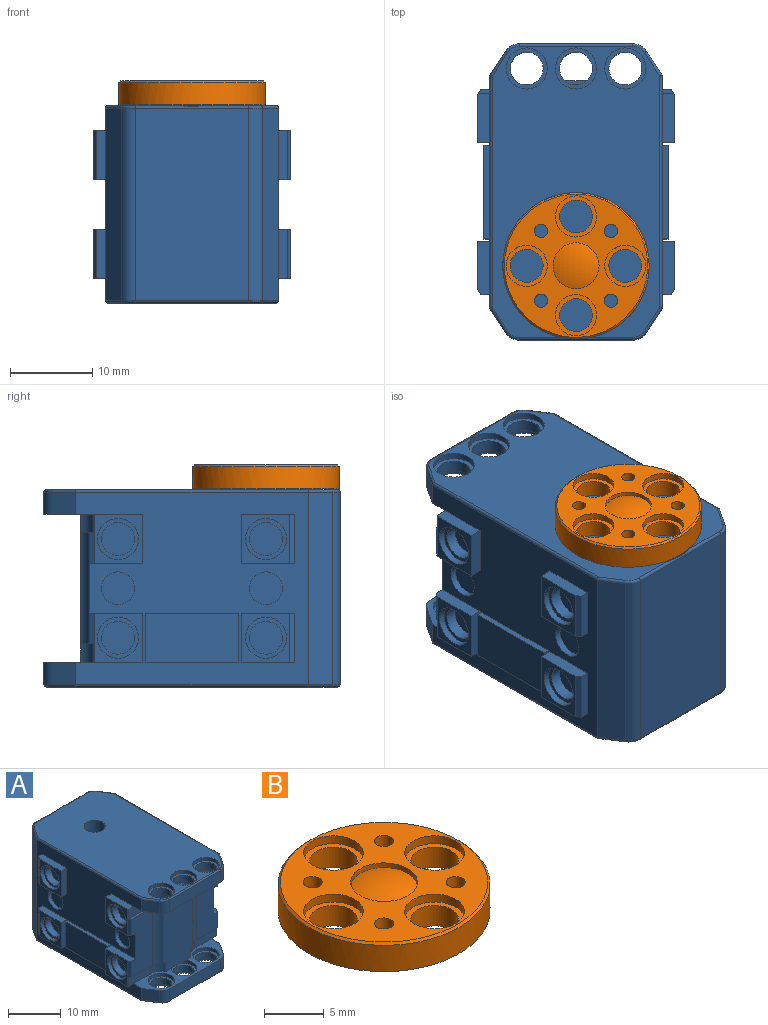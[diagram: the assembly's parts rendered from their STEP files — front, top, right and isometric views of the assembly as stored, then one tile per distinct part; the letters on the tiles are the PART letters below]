
ASSEMBLY  parts=2 mates=1
PART A: 203 faces, bbox 24x36x24 mm
  f0: cylinder r=8.9mm len=3.75mm, axis (0,0,1), area 0mm2, adj f1,f138
  f1: plane 35.6x20.4mm, normal (0,0,1), area 633.5mm2, adj f0,f38,f39,f40,f42,f43,f44,f61
  f2: plane 4x4mm, normal (1,0,0), area 12.6mm2, adj f10
  f3: plane 4x4mm, normal (1,0,0), area 12.6mm2, adj f11
  f4: plane 4x4mm, normal (1,0,0), area 12.6mm2, adj f12
  f5: plane 4x4mm, normal (1,0,0), area 12.6mm2, adj f13
  f6: plane 4x4mm, normal (-1,0,0), area 12.6mm2, adj f14
  f7: plane 4x4mm, normal (-1,0,0), area 12.6mm2, adj f15
  f8: plane 4x4mm, normal (-1,0,0), area 12.6mm2, adj f16
  f9: plane 4x4mm, normal (-1,0,0), area 12.6mm2, adj f17
  f10: cylinder r=2mm len=4mm, axis (1,0,0), area 17.6mm2, adj f2,f18
  f11: cylinder r=2mm len=4mm, axis (1,0,0), area 17.6mm2, adj f3,f19
  f12: cylinder r=2mm len=4mm, axis (1,0,0), area 17.6mm2, adj f4,f20
  f13: cylinder r=2mm len=4mm, axis (1,0,0), area 17.6mm2, adj f5,f21
  f14: cylinder r=2mm len=4mm, axis (1,0,0), area 17.6mm2, adj f6,f28
  f15: cylinder r=2mm len=4mm, axis (1,0,0), area 17.6mm2, adj f7,f29
  f16: cylinder r=2mm len=4mm, axis (1,0,0), area 17.6mm2, adj f8,f31
  f17: cylinder r=2mm len=4mm, axis (1,0,0), area 17.6mm2, adj f9,f32
  f18: plane 5x5mm, normal (1,0,0), area 7.1mm2, adj f10,f34
  f19: plane 5x5mm, normal (1,0,0), area 7.1mm2, adj f11,f35
  f20: plane 5x5mm, normal (1,0,0), area 7.1mm2, adj f12,f36
  f21: plane 5x5mm, normal (1,0,0), area 7.1mm2, adj f13,f37
  f22: plane 5x5mm, normal (0,0,1), area 7.1mm2, adj f26,f38
  f23: plane 5x5mm, normal (0,0,1), area 7.1mm2, adj f25,f39
  f24: plane 5x5mm, normal (0,0,1), area 7.1mm2, adj f27,f40
  f25: cylinder r=2mm len=4mm, axis (0,0,1), area 17.6mm2, adj f23,f41
  f26: cylinder r=2mm len=4mm, axis (0,0,1), area 17.6mm2, adj f22,f45
  f27: cylinder r=2mm len=4mm, axis (0,0,1), area 17.6mm2, adj f24,f46
  f28: plane 5x5mm, normal (-1,0,0), area 7.1mm2, adj f14,f47
  f29: plane 5x5mm, normal (-1,0,0), area 7.1mm2, adj f15,f48
  f30: plane 4x1mm, normal (0,0,1), area 2.8mm2, adj f49,f74
  f31: plane 5x5mm, normal (-1,0,0), area 7.1mm2, adj f16,f50
  f32: plane 5x5mm, normal (-1,0,0), area 7.1mm2, adj f17,f51
  f33: plane 4x1mm, normal (0,0,-1), area 2.8mm2, adj f49,f91
  f34: cylinder r=2.5mm len=5mm, axis (1,0,0), area 12.6mm2, adj f18,f54
  f35: cylinder r=2.5mm len=5mm, axis (1,0,0), area 12.6mm2, adj f19,f60
  f36: cylinder r=2.5mm len=5mm, axis (1,0,0), area 12.6mm2, adj f20,f63
  f37: cylinder r=2.5mm len=5mm, axis (1,0,0), area 12.6mm2, adj f21,f65
  f38: cylinder r=2.5mm len=5mm, axis (0,0,1), area 12.6mm2, adj f1,f22
  f39: cylinder r=2.5mm len=5mm, axis (0,0,1), area 12.6mm2, adj f1,f23
  f40: cylinder r=2.5mm len=5mm, axis (0,0,1), area 12.6mm2, adj f1,f24
  f41: plane 5x5mm, normal (0,0,-1), area 7.1mm2, adj f25,f74
  f42: revolved ~1.68x1.07mm, area 0.9mm2, adj f1,f43,f73,f77
  f43: cylinder r=0.3mm len=13.83mm, axis (1,0,0), area 6.5mm2, adj f1,f42,f44,f78
  f44: revolved ~1.68x1.07mm, area 0.9mm2, adj f1,f43,f61,f79
  f45: plane 5x5mm, normal (0,0,-1), area 7.1mm2, adj f26,f82
  f46: plane 5x5mm, normal (0,0,-1), area 7.1mm2, adj f27,f83
  f47: cylinder r=2.5mm len=5mm, axis (1,0,0), area 12.6mm2, adj f28,f84
  f48: cylinder r=2.5mm len=5mm, axis (1,0,0), area 12.6mm2, adj f29,f90
  f49: plane 18x8mm, normal (0,-1,0), area 138.4mm2, adj f30,f33,f56,f57,f58,f75,f81,f86
  f50: cylinder r=2.5mm len=5mm, axis (1,0,0), area 12.6mm2, adj f31,f99
  f51: cylinder r=2.5mm len=5mm, axis (1,0,0), area 12.6mm2, adj f32,f101
  f52: revolved ~1.68x1.07mm, area 0.9mm2, adj f111,f186,f187,f200
  f53: revolved ~1.68x1.07mm, area 0.9mm2, adj f112,f187,f188,f200
  f54: plane 6x5.84mm, normal (1,0,0), area 15.4mm2, adj f34,f59,f114,f115,f116
  f55: plane 6x0.66mm, normal (0.84,-0.54,0), area 3.3mm2, adj f56,f60,f80,f117,f118,f120
  f56: plane 8.54x1.53mm, normal (0,0,1), area 4.5mm2, adj f49,f55,f57,f80,f81,f117
  f57: cylinder r=2.5mm len=13.5mm, axis (0,0,1), area 31.3mm2, adj f49,f56,f58,f117
  f58: plane 8.54x1.53mm, normal (0,0,-1), area 4.5mm2, adj f49,f57,f59,f94,f95,f117
  f59: plane 6x0.66mm, normal (0.84,-0.54,0), area 3.3mm2, adj f54,f58,f94,f114,f116,f117
  f60: plane 6x5.84mm, normal (1,0,0), area 15.4mm2, adj f35,f55,f118,f119,f120
  f61: cylinder r=0.3mm len=3.1mm, axis (0.54,0.84,0), area 1.6mm2, adj f1,f44,f113,f121
  f62: plane 6x0.66mm, normal (0.84,0.54,0), area 4.7mm2, adj f63,f122,f123,f124
  f63: plane 6x5.84mm, normal (1,0,0), area 15.4mm2, adj f36,f62,f122,f124,f125
  f64: plane 6x0.66mm, normal (0.84,0.54,0), area 4.7mm2, adj f65,f126,f127,f128
  f65: plane 6x5.84mm, normal (1,0,0), area 15.4mm2, adj f37,f64,f126,f128,f129
  f66: plane 4x4mm, normal (1,0,0), area 12.6mm2, adj f130
  f67: plane 4x4mm, normal (1,0,0), area 12.6mm2, adj f131
  f68: plane 11.4x6mm, normal (1,0,0), area 68.4mm2, adj f132,f133,f134,f135
  f69: revolved ~1.68x1.07mm, area 0.9mm2, adj f137,f190,f191,f200
  f70: revolved ~1.68x1.07mm, area 0.9mm2, adj f1,f136,f137,f138
  f71: revolved ~1.68x1.07mm, area 0.9mm2, adj f139,f191,f192,f200
  f72: revolved ~1.68x1.07mm, area 0.9mm2, adj f1,f138,f139,f140
  f73: cylinder r=0.3mm len=3.1mm, axis (0.54,-0.84,0), area 1.6mm2, adj f1,f42,f141,f142
  f74: cylinder r=2.5mm len=5mm, axis (0,0,1), area 12.6mm2, adj f30,f41,f143
  f75: cylinder r=3.02mm len=2.63mm, axis (0,0,1), area 7.2mm2, adj f49,f76,f88,f143
  f76: plane 5.91x2.25mm, normal (0,-1,0), area 13.3mm2, adj f75,f88,f89,f143,f144
  f77: cylinder r=2mm len=2.7mm, axis (0,0,1), area 5.4mm2, adj f42,f78,f142,f143
  f78: plane 13.83x2.7mm, normal (0,-1,0), area 37.3mm2, adj f43,f77,f79,f143
  f79: cylinder r=2mm len=2.7mm, axis (0,0,1), area 5.4mm2, adj f44,f78,f121,f143
  f80: plane 5.91x2.25mm, normal (0,-1,0), area 13.3mm2, adj f55,f56,f81,f120,f143
  f81: cylinder r=3.02mm len=2.63mm, axis (0,0,1), area 7.2mm2, adj f49,f56,f80,f143
  f82: cylinder r=2.5mm len=5mm, axis (0,0,1), area 12.6mm2, adj f45,f143
  f83: cylinder r=2.5mm len=5mm, axis (0,0,1), area 12.6mm2, adj f46,f143
  f84: plane 6x5.84mm, normal (-1,0,0), area 15.4mm2, adj f47,f89,f144,f145,f146
  f85: plane 6x0.66mm, normal (-0.84,-0.54,0), area 3.3mm2, adj f86,f90,f93,f147,f148,f150
  f86: plane 8.54x1.53mm, normal (0,0,-1), area 4.5mm2, adj f49,f85,f87,f92,f93,f147
  f87: cylinder r=2.5mm len=13.5mm, axis (0,0,1), area 31.3mm2, adj f49,f86,f88,f147
  f88: plane 8.54x1.53mm, normal (0,0,1), area 4.5mm2, adj f49,f75,f76,f87,f89,f147
  f89: plane 6x0.66mm, normal (-0.84,-0.54,0), area 3.3mm2, adj f76,f84,f88,f144,f146,f147
  f90: plane 6x5.84mm, normal (-1,0,0), area 15.4mm2, adj f48,f85,f148,f149,f150
  f91: cylinder r=2.5mm len=5mm, axis (0,0,1), area 12.6mm2, adj f33,f109,f151
  f92: cylinder r=3.02mm len=2.63mm, axis (0,0,1), area 7.2mm2, adj f49,f86,f93,f151
  f93: plane 5.91x2.25mm, normal (0,-1,0), area 13.3mm2, adj f85,f86,f92,f150,f151
  f94: plane 5.91x2.25mm, normal (0,-1,0), area 13.3mm2, adj f58,f59,f95,f114,f151
  f95: cylinder r=3.02mm len=2.63mm, axis (0,0,1), area 7.2mm2, adj f49,f58,f94,f151
  f96: cylinder r=2.5mm len=5mm, axis (0,0,1), area 12.6mm2, adj f108,f151
  f97: cylinder r=2.5mm len=5mm, axis (0,0,1), area 12.6mm2, adj f110,f151
  f98: plane 6x0.66mm, normal (-0.84,0.54,0), area 4.7mm2, adj f99,f152,f153,f154
  f99: plane 6x5.84mm, normal (-1,0,0), area 15.4mm2, adj f50,f98,f152,f154,f155
  f100: plane 6x0.66mm, normal (-0.84,0.54,0), area 4.7mm2, adj f101,f156,f157,f158
  f101: plane 6x5.84mm, normal (-1,0,0), area 15.4mm2, adj f51,f100,f156,f158,f159
  f102: plane 4x4mm, normal (-1,0,0), area 12.6mm2, adj f160
  f103: plane 4x4mm, normal (-1,0,0), area 12.6mm2, adj f161
  f104: plane 11.4x6mm, normal (-1,0,0), area 68.4mm2, adj f162,f163,f164,f165
  f105: plane 4x4mm, normal (0,0,-1), area 12.6mm2, adj f166
  f106: plane 4x4mm, normal (0,0,-1), area 12.6mm2, adj f167
  f107: plane 4x4mm, normal (0,0,-1), area 12.6mm2, adj f168
  f108: plane 5x5mm, normal (0,0,1), area 7.1mm2, adj f96,f169
  f109: plane 5x5mm, normal (0,0,1), area 7.1mm2, adj f91,f170
  f110: plane 5x5mm, normal (0,0,1), area 7.1mm2, adj f97,f171
  f111: cylinder r=2mm len=2.7mm, axis (0,0,1), area 5.4mm2, adj f52,f151,f172,f173
  f112: cylinder r=2mm len=2.7mm, axis (0,0,1), area 5.4mm2, adj f53,f151,f173,f174
  f113: cylinder r=0.3mm len=28.3mm, axis (0,1,0), area 13.3mm2, adj f1,f61,f136,f175
  f114: plane 5.98x1.5mm, normal (0,0,-1), area 9mm2, adj f54,f59,f94,f115,f175
  f115: plane 6x1.5mm, normal (0,1,0), area 9mm2, adj f54,f114,f116,f175
  f116: plane 6.5x1.5mm, normal (0,0,1), area 9.6mm2, adj f54,f59,f115,f117,f175
  f117: plane 13.5x5.57mm, normal (0,-1,0), area 68.8mm2, adj f55,f56,f57,f58,f59,f116,f118,f175
  f118: plane 6.5x1.5mm, normal (0,0,-1), area 9.6mm2, adj f55,f60,f117,f119,f175
  f119: plane 6x1.5mm, normal (0,1,0), area 9mm2, adj f60,f118,f120,f175
  f120: plane 5.98x1.5mm, normal (0,0,1), area 9mm2, adj f55,f60,f80,f119,f175
  f121: plane 2.94x2.7mm, normal (0.84,-0.54,0), area 9.5mm2, adj f61,f79,f143,f175
  f122: plane 6.5x1.5mm, normal (0,0,-1), area 9.6mm2, adj f62,f63,f123,f125,f175
  f123: plane 6x1.07mm, normal (0,1,0), area 6.4mm2, adj f62,f122,f124,f175
  f124: plane 6.5x1.5mm, normal (0,0,1), area 9.6mm2, adj f62,f63,f123,f125,f175
  f125: plane 6x1.5mm, normal (0,-1,0), area 9mm2, adj f63,f122,f124,f175
  f126: plane 6.5x1.5mm, normal (0,0,-1), area 9.6mm2, adj f64,f65,f127,f129,f175
  f127: plane 6x1.07mm, normal (0,1,0), area 6.4mm2, adj f64,f126,f128,f175
  f128: plane 6.5x1.5mm, normal (0,0,1), area 9.6mm2, adj f64,f65,f127,f129,f175
  f129: plane 6x1.5mm, normal (0,-1,0), area 9mm2, adj f65,f126,f128,f175
  f130: cylinder r=2mm len=4mm, axis (1,0,0), area 10.1mm2, adj f66,f175
  f131: cylinder r=2mm len=4mm, axis (1,0,0), area 10.1mm2, adj f67,f175
  f132: plane 11.4x0.7mm, normal (0,0,1), area 8mm2, adj f68,f133,f135,f175
  f133: plane 6x0.7mm, normal (0,-1,0), area 4.2mm2, adj f68,f132,f134,f175
  f134: plane 11.4x0.7mm, normal (0,0,-1), area 8mm2, adj f68,f133,f135,f175
  f135: plane 6x0.7mm, normal (0,1,0), area 4.2mm2, adj f68,f132,f134,f175
  f136: cylinder r=0.3mm len=3.1mm, axis (-0.54,0.84,0), area 1.6mm2, adj f1,f70,f113,f176
  f137: cylinder r=2mm len=23.4mm, axis (0,0,-1), area 46.6mm2, adj f69,f70,f176,f177
  f138: cylinder r=0.3mm len=13.83mm, axis (-1,0,0), area 6mm2, adj f0,f1,f70,f72,f177
  f139: cylinder r=2mm len=23.4mm, axis (0,0,-1), area 46.6mm2, adj f71,f72,f177,f178
  f140: cylinder r=0.3mm len=3.1mm, axis (-0.54,-0.84,0), area 1.6mm2, adj f1,f72,f141,f178
  f141: cylinder r=0.3mm len=28.3mm, axis (0,-1,0), area 13.3mm2, adj f1,f73,f140,f179
  f142: plane 2.94x2.7mm, normal (-0.84,-0.54,0), area 9.5mm2, adj f73,f77,f143,f179
  f143: plane 21x6.03mm, normal (0,0,-1), area 47.8mm2, adj f49,f74,f75,f76,f77,f78,f79,f80
  f144: plane 5.98x1.5mm, normal (0,0,1), area 9mm2, adj f76,f84,f89,f145,f179
  f145: plane 6x1.5mm, normal (0,1,0), area 9mm2, adj f84,f144,f146,f179
  f146: plane 6.5x1.5mm, normal (0,0,-1), area 9.6mm2, adj f84,f89,f145,f147,f179
  f147: plane 13.5x5.57mm, normal (0,-1,0), area 68.8mm2, adj f85,f86,f87,f88,f89,f146,f148,f179
  f148: plane 6.5x1.5mm, normal (0,0,1), area 9.6mm2, adj f85,f90,f147,f149,f179
  f149: plane 6x1.5mm, normal (0,1,0), area 9mm2, adj f90,f148,f150,f179
  f150: plane 5.98x1.5mm, normal (0,0,-1), area 9mm2, adj f85,f90,f93,f149,f179
  f151: plane 21x6.03mm, normal (0,0,1), area 47.8mm2, adj f49,f91,f92,f93,f94,f95,f96,f97
  f152: plane 6.5x1.5mm, normal (0,0,1), area 9.6mm2, adj f98,f99,f153,f155,f179
  f153: plane 6x1.07mm, normal (0,1,0), area 6.4mm2, adj f98,f152,f154,f179
  f154: plane 6.5x1.5mm, normal (0,0,-1), area 9.6mm2, adj f98,f99,f153,f155,f179
  f155: plane 6x1.5mm, normal (0,-1,0), area 9mm2, adj f99,f152,f154,f179
  f156: plane 6.5x1.5mm, normal (0,0,1), area 9.6mm2, adj f100,f101,f157,f159,f179
  f157: plane 6x1.07mm, normal (0,1,0), area 6.4mm2, adj f100,f156,f158,f179
  f158: plane 6.5x1.5mm, normal (0,0,-1), area 9.6mm2, adj f100,f101,f157,f159,f179
  f159: plane 6x1.5mm, normal (0,-1,0), area 9mm2, adj f101,f156,f158,f179
  f160: cylinder r=2mm len=4mm, axis (1,0,0), area 10.1mm2, adj f102,f179
  f161: cylinder r=2mm len=4mm, axis (1,0,0), area 10.1mm2, adj f103,f179
  f162: plane 11.4x0.7mm, normal (0,0,1), area 8mm2, adj f104,f163,f165,f179
  f163: plane 6x0.7mm, normal (0,1,0), area 4.2mm2, adj f104,f162,f164,f179
  f164: plane 11.4x0.7mm, normal (0,0,-1), area 8mm2, adj f104,f163,f165,f179
  f165: plane 6x0.7mm, normal (0,-1,0), area 4.2mm2, adj f104,f162,f164,f179
  f166: cylinder r=2mm len=4mm, axis (0,0,-1), area 27.6mm2, adj f105,f180
  f167: cylinder r=2mm len=4mm, axis (0,0,-1), area 27.6mm2, adj f106,f181
  f168: cylinder r=2mm len=4mm, axis (0,0,-1), area 27.6mm2, adj f107,f182
  f169: cylinder r=2mm len=4mm, axis (0,0,1), area 17.6mm2, adj f108,f183
  f170: cylinder r=2mm len=4mm, axis (0,0,1), area 17.6mm2, adj f109,f184
  f171: cylinder r=2mm len=4mm, axis (0,0,1), area 17.6mm2, adj f110,f185
  f172: plane 2.94x2.7mm, normal (-0.84,-0.54,0), area 9.5mm2, adj f111,f151,f179,f186
  f173: plane 13.83x2.7mm, normal (0,-1,0), area 37.3mm2, adj f111,f112,f151,f187
  f174: plane 2.94x2.7mm, normal (0.84,-0.54,0), area 9.5mm2, adj f112,f151,f175,f188
  f175: plane 28.3x23.4mm, normal (1,0,0), area 383mm2, adj f113,f114,f115,f116,f117,f118,f119,f120
  f176: plane 23.4x2.94mm, normal (0.84,0.54,0), area 82mm2, adj f136,f137,f175,f190
  f177: plane 23.4x13.83mm, normal (0,1,0), area 323.6mm2, adj f137,f138,f139,f191
  f178: plane 23.4x2.94mm, normal (-0.84,0.54,0), area 82mm2, adj f139,f140,f179,f192
  f179: plane 28.3x23.4mm, normal (-1,0,0), area 383mm2, adj f141,f142,f143,f144,f145,f146,f147,f148
  f180: plane 5x5mm, normal (0,0,-1), area 7.1mm2, adj f166,f194
  f181: plane 5x5mm, normal (0,0,-1), area 7.1mm2, adj f167,f195
  f182: plane 5x5mm, normal (0,0,-1), area 7.1mm2, adj f168,f196
  f183: plane 5x5mm, normal (0,0,-1), area 7.1mm2, adj f169,f197
  f184: plane 5x5mm, normal (0,0,-1), area 7.1mm2, adj f170,f198
  f185: plane 5x5mm, normal (0,0,-1), area 7.1mm2, adj f171,f199
  f186: cylinder r=0.3mm len=3.1mm, axis (-0.54,0.84,0), area 1.6mm2, adj f52,f172,f193,f200
  f187: cylinder r=0.3mm len=13.83mm, axis (-1,0,0), area 6.5mm2, adj f52,f53,f173,f200
  f188: cylinder r=0.3mm len=3.1mm, axis (-0.54,-0.84,0), area 1.6mm2, adj f53,f174,f189,f200
  f189: cylinder r=0.3mm len=28.3mm, axis (0,-1,0), area 13.3mm2, adj f175,f188,f190,f200
  f190: cylinder r=0.3mm len=3.1mm, axis (0.54,-0.84,0), area 1.6mm2, adj f69,f176,f189,f200
  f191: cylinder r=0.3mm len=13.83mm, axis (1,0,0), area 6.5mm2, adj f69,f71,f177,f200
  f192: cylinder r=0.3mm len=3.1mm, axis (0.54,0.84,0), area 1.6mm2, adj f71,f178,f193,f200
  f193: cylinder r=0.3mm len=28.3mm, axis (0,1,0), area 13.3mm2, adj f179,f186,f192,f200
  f194: cylinder r=2.5mm len=5mm, axis (0,0,-1), area 12.6mm2, adj f180,f200
  f195: cylinder r=2.5mm len=5mm, axis (0,0,-1), area 12.6mm2, adj f181,f200
  f196: cylinder r=2.5mm len=5mm, axis (0,0,-1), area 12.6mm2, adj f182,f200
  f197: cylinder r=2.5mm len=5mm, axis (0,0,-1), area 12.6mm2, adj f183,f200
  f198: cylinder r=2.5mm len=5mm, axis (0,0,-1), area 12.6mm2, adj f184,f200
  f199: cylinder r=2.5mm len=5mm, axis (0,0,-1), area 12.6mm2, adj f185,f200
  f200: plane 35.4x20.4mm, normal (0,0,-1), area 586.6mm2, adj f52,f53,f69,f71,f186,f187,f188,f189
  f201: cylinder r=2mm len=5mm, axis (0,0,1), area 62.8mm2, adj f1,f202
  f202: plane 4x4mm, normal (0,0,1), area 12.6mm2, adj f201
PART B: 22 faces, bbox 17.8x17.8x2.9 mm
  f0: revolved ~5.62x5.6mm, area 25.4mm2, adj f13
  f1: plane 5x5mm, normal (0,0,1), area 7.1mm2, adj f2,f3
  f2: cylinder r=2mm len=4mm, axis (0,0,1), area 26.4mm2, adj f1,f21
  f3: cylinder r=2.5mm len=5mm, axis (0,0,1), area 12.6mm2, adj f1,f19
  f4: plane 5x5mm, normal (0,0,1), area 7.1mm2, adj f5,f6
  f5: cylinder r=2mm len=4mm, axis (0,0,1), area 26.4mm2, adj f4,f21
  f6: cylinder r=2.5mm len=5mm, axis (0,0,1), area 12.6mm2, adj f4,f19
  f7: plane 5x5mm, normal (0,0,1), area 7.1mm2, adj f8,f9
  f8: cylinder r=2mm len=4mm, axis (0,0,1), area 26.4mm2, adj f7,f21
  f9: cylinder r=2.5mm len=5mm, axis (0,0,1), area 12.6mm2, adj f7,f19
  f10: plane 5x5mm, normal (0,0,1), area 7.1mm2, adj f11,f12
  f11: cylinder r=2mm len=4mm, axis (0,0,1), area 26.4mm2, adj f10,f21
  f12: cylinder r=2.5mm len=5mm, axis (0,0,1), area 12.6mm2, adj f10,f19
  f13: cylinder r=2.8mm len=5.6mm, axis (0,0,1), area 8.8mm2, adj f0,f19
  f14: cone r=8.9mm half-angle=45deg, axis (0,0,-1), area 15.6mm2, adj f15,f19
  f15: cylinder r=8.9mm len=17.8mm, axis (0,0,1), area 151mm2, adj f14,f21
  f16: cylinder r=0.8mm len=2.9mm, axis (0,0,1), area 14.6mm2, adj f19,f21
  f17: cylinder r=0.8mm len=2.9mm, axis (0,0,1), area 14.6mm2, adj f19,f21
  f18: cylinder r=0.8mm len=2.9mm, axis (0,0,1), area 14.6mm2, adj f19,f21
  f19: plane 17.4x17.4mm, normal (0,0,1), area 126.6mm2, adj f3,f6,f9,f12,f13,f14,f16,f17
  f20: cylinder r=0.8mm len=2.9mm, axis (0,0,1), area 14.6mm2, adj f19,f21
  f21: plane 17.8x17.8mm, normal (0,0,-1), area 190.5mm2, adj f2,f5,f8,f11,f15,f16,f17,f18
PLACE A rot(axis=(0,0,1),180deg) t=(0,0,12)mm
PLACE B t=(0,0,12)mm
MATE revolute B.f13 <-> A.f0  axis (0,0,1) through (0,0,24.1)mm
